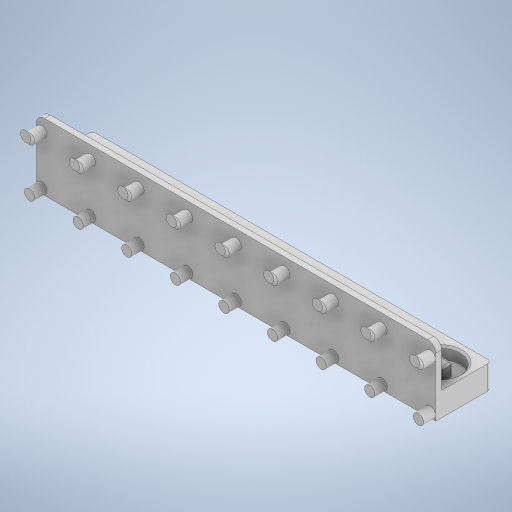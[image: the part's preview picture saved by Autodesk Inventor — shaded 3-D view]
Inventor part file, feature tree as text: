
AUTODESK INVENTOR PART (.ipt)
format: ipt  version: 2024 (Build 280153000, 153)  size: 1,403,904 bytes
history: native  units: mm
features: other x16, projected_geometry x14, extrude x10, sketch x10, fillet x4, pattern_linear x3, loft x1, chamfer x1
ambient origin geometry x8: Origin, YZ Plane, XZ Plane, XY Plane, X Axis, Y Axis, Z Axis, Center Point
bodies: Body1 (feature_tree)
feature tree (59):
  other  "Твердое тело1"
  extrude  "Выдавливание1"  Depth=1.85mm TaperAngle=0.0deg
  extrude  "Выдавливание2"  Depth=204.9mm
  pattern_linear  "Прямоуг.массив1"  Spacing1=32.25mm  [1 undecoded]
  extrude  "Выдавливание3"  Depth=5.3mm
  extrude  "Выдавливание4"  Depth=6.2mm TaperAngle=0.0deg
  fillet  "Сопряжение1"  Radius=20.0mm
  pattern_linear  "Прямоуг.массив2"  Spacing1=24.95mm  [1 undecoded]
  fillet  "Сопряжение2"  Radius=15.0mm
  other  "РабПлоскость1"
  loft  "Лофт1"
  pattern_linear  "Прямоуг.массив3"  Count1=20  [1 undecoded]
  other  "Удаление грани1"
  sketch  "Эскиз10"
  extrude  "Выдавливание6"  Depth=13.0mm
  extrude  "Выдавливание7"  TaperAngle=0.0deg  [1 undecoded]
  extrude  "Выдавливание8"  Depth=18.0mm
  extrude  "Выдавливание9"  Depth=2.0mm
  other  "Непосредственное редактирование1"
  other  "Непосредственное редактирование2"
  chamfer  "Фаска3"  Distance=10.0mm
  extrude  "Выдавливание11"  Depth=10.0mm
  other  "Непосредственное редактирование3"
  other  "Непосредственное редактирование4"
  fillet  "Сопряжение5"  Radius=20.4mm
  fillet  "Сопряжение6"  Radius=2.0mm
  other  "Непосредственное редактирование5"
  other  "Непосредственное редактирование6"
  extrude  "Выдавливание12"  Depth=204.8mm
  sketch  "Эскиз1"
  sketch  "Эскиз2"
  sketch  "Эскиз3"
  sketch  "Эскиз4"
  sketch  "Эскиз7"
  other  "Ребра1"
  sketch  "Эскиз11"
  projected_geometry  "Спроецированная петля4"
  sketch  "Эскиз12"
  sketch  "Эскиз14"
  sketch  "Эскиз15"
  projected_geometry  "Спроецированная петля7"
  projected_geometry  "Спроецированная петля8"
  projected_geometry  "Спроецированная петля9"
  projected_geometry  "Спроецированная петля10"
  projected_geometry  "Спроецированная петля11"
  projected_geometry  "Спроецированная петля12"
  projected_geometry  "Спроецированная петля13"
  projected_geometry  "Спроецированная петля14"
  projected_geometry  "Спроецированная петля15"
  projected_geometry  "Спроецированная петля16"
  projected_geometry  "Спроецированная петля17"
  projected_geometry  "Спроецированная петля18"
  projected_geometry  "Спроецированная петля19"
  other  "Перенос1"
  other  "Перенос2"
  other  "Перенос3"
  other  "Перенос4"
  other  "Перенос5"
  other  "Перенос6"
note: 4 required parameter values undecoded (feature->parameter linkage not recoverable at this tier; creation-order binding heuristic only, values carry confidence <= 0.55)
